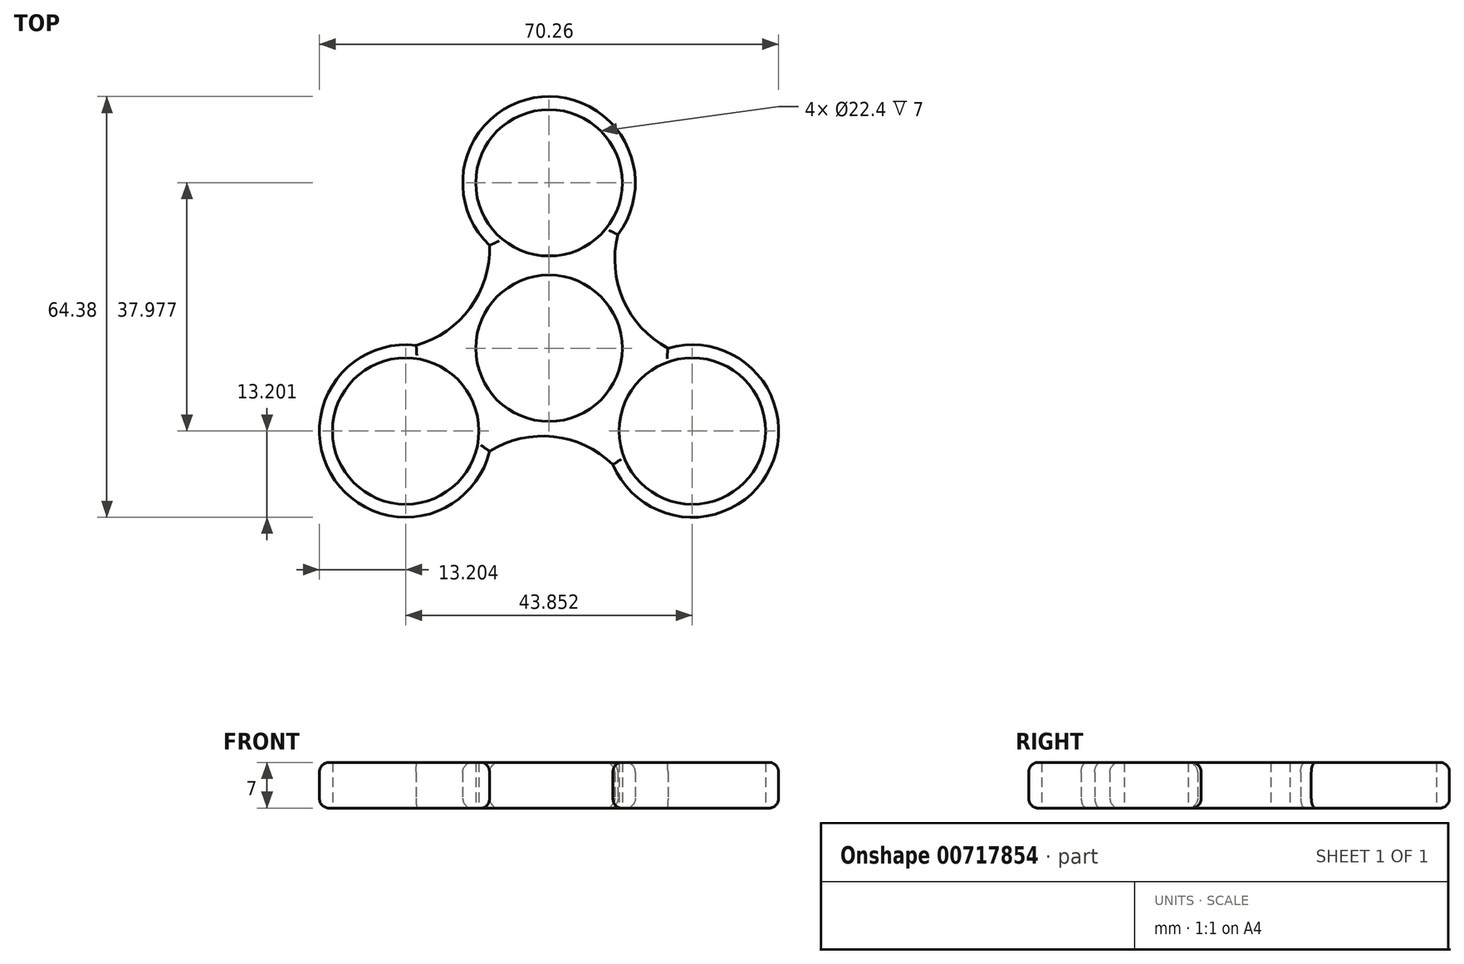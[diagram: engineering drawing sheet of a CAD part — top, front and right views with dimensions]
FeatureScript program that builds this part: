
annotation { "Feature Type Name" : "Feature", "Feature Type Description" : "" }
export const myFeature = defineFeature(function(context is Context, id is Id, definition is map)
    precondition{}
    {
        {
            var Q0;
            Q0=qCreatedBy(makeId("Top.planeOp"),FACE);
            var sketch = newSketch(context, id + "F0", { "sketchPlane" : qUnion([Q0])});
            skCircle(sketch, "E0", {"center": v(0, 0) * mm, "radius": 11.2 * mm});
            skCircle(sketch, "E1", {"center": v(0, 25.32) * mm, "radius": 11.2 * mm});
            skArc(sketch, "E2", {"start": v(10.55, 17.38) * mm, "mid": v(-1.1, 38.47) * mm, "end": v(-9.1, 15.75) * mm});
            skCircle(sketch, "E3.1.0", {"center": v(-21.93, -12.66) * mm, "radius": 11.2 * mm});
            skArc(sketch, "E3.1.1", {"start": v(-20.32, 0.44) * mm, "mid": v(-32.77, -20.18) * mm, "end": v(-9.1, -15.75) * mm});
            skCircle(sketch, "E3.2.0", {"center": v(21.93, -12.66) * mm, "radius": 11.2 * mm});
            skArc(sketch, "E3.2.1", {"start": v(9.78, -17.82) * mm, "mid": v(33.86, -18.3) * mm, "end": v(18.19, 0) * mm});
            skArc(sketch, "E4", {"start": v(10.55, 17.38) * mm, "mid": v(11.37, 7.37) * mm, "end": v(18.19, 0) * mm});
            skArc(sketch, "E5.1.0", {"start": v(-20.32, 0.44) * mm, "mid": v(-12.07, 6.16) * mm, "end": v(-9.1, 15.75) * mm});
            skArc(sketch, "E5.2.0", {"start": v(9.78, -17.82) * mm, "mid": v(0.7, -13.53) * mm, "end": v(-9.1, -15.75) * mm});
            skSolve(sketch);
        }
        {
            var Q0;
            Q0 = qSketchRegion(id + "F0", true);
            extrude(context, id + "F1", {"entities" : qUnion([Q0]), "depth" : 7 * mm, "offsetDistance" : 25 * mm});
        }
        {
            var Q0;
            Q0=makeQuery(id+"F1.opExtrude","CAP_EDGE",EDGE,{"disambiguationData":[OSD([sQuery(id+"F0.wireOp",EDGE,"E2")])],"isStart":false});
            var Q1;
            Q1=makeQuery(id+"F1.opExtrude","CAP_EDGE",EDGE,{"disambiguationData":[OSD([sQuery(id+"F0.wireOp",EDGE,"E5.1.0")])],"isStart":false});
            var Q2;
            Q2=makeQuery(id+"F1.opExtrude","CAP_EDGE",EDGE,{"disambiguationData":[OSD([sQuery(id+"F0.wireOp",EDGE,"E4")])],"isStart":false});
            var Q3;
            Q3=makeQuery(id+"F1.opExtrude","CAP_EDGE",EDGE,{"disambiguationData":[OSD([sQuery(id+"F0.wireOp",EDGE,"E3.2.1")])],"isStart":false});
            var Q4;
            Q4=makeQuery(id+"F1.opExtrude","CAP_EDGE",EDGE,{"disambiguationData":[OSD([sQuery(id+"F0.wireOp",EDGE,"E5.2.0")])],"isStart":false});
            var Q5;
            Q5=makeQuery(id+"F1.opExtrude","CAP_EDGE",EDGE,{"disambiguationData":[OSD([sQuery(id+"F0.wireOp",EDGE,"E3.1.1")])],"isStart":false});
            fillet(context, id + "F2", {"entities" : qUnion([Q0, Q1, Q2, Q3, Q4, Q5]), "radius" : 1.5 * mm, "tangentPropagation" : true, "allowEdgeOverflow" : false});
        }
        {
            var Q0;
            Q0=makeQuery(id+"F1.opExtrude","CAP_EDGE",EDGE,{"disambiguationData":[OSD([sQuery(id+"F0.wireOp",EDGE,"E3.1.1")])],"isStart":true});
            var Q1;
            Q1=makeQuery(id+"F1.opExtrude","CAP_EDGE",EDGE,{"disambiguationData":[OSD([sQuery(id+"F0.wireOp",EDGE,"E5.2.0")])],"isStart":true});
            var Q2;
            Q2=makeQuery(id+"F1.opExtrude","CAP_EDGE",EDGE,{"disambiguationData":[OSD([sQuery(id+"F0.wireOp",EDGE,"E5.1.0")])],"isStart":true});
            var Q3;
            Q3=makeQuery(id+"F1.opExtrude","CAP_EDGE",EDGE,{"disambiguationData":[OSD([sQuery(id+"F0.wireOp",EDGE,"E2")])],"isStart":true});
            var Q4;
            Q4=makeQuery(id+"F1.opExtrude","CAP_EDGE",EDGE,{"disambiguationData":[OSD([sQuery(id+"F0.wireOp",EDGE,"E4")])],"isStart":true});
            var Q5;
            Q5=makeQuery(id+"F1.opExtrude","CAP_EDGE",EDGE,{"disambiguationData":[OSD([sQuery(id+"F0.wireOp",EDGE,"E3.2.1")])],"isStart":true});
            fillet(context, id + "F3", {"entities" : qUnion([Q0, Q1, Q2, Q3, Q4, Q5]), "radius" : 1.5 * mm, "tangentPropagation" : true, "allowEdgeOverflow" : false});
        }
    });
